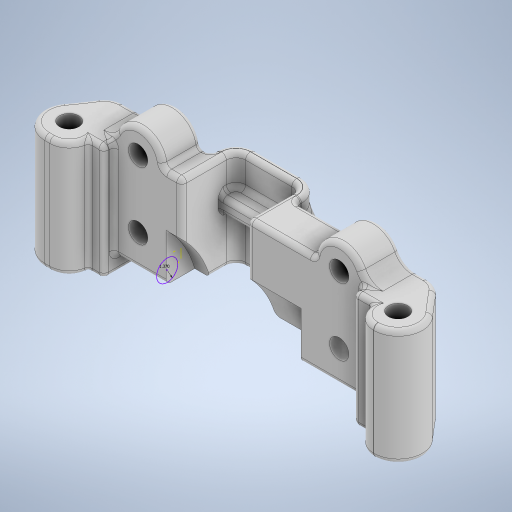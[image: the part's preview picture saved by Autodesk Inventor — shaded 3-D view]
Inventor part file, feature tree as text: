
AUTODESK INVENTOR PART (.ipt)
format: ipt  version: 2024 (Build 280153000, 153)  size: 1,158,656 bytes
history: native  units: in
note: dims shown in document units (in); Inventor stores cm internally (conversion verified against a paired STEP export)
features: fillet x17, sketch x16, extrude x13, pattern_linear x2, hole x2, projected_geometry x2, plane x1, rib x1, direct_edit x1, other x1
ambient origin geometry x8: Origin, YZ Plane, XZ Plane, XY Plane, X Axis, Y Axis, Z Axis, Center Point
bodies: Solid1 (feature_tree)
feature tree (56):
  extrude  "Extrusion1"  Depth=0.415in
  extrude  "Extrusion2"  Depth=1.62in
  fillet  "Fillet1"  Radius=0.315in
  extrude  "Extrusion3"  Depth=0.125in TaperAngle=0.0deg
  extrude  "Extrusion4"  TaperAngle=0.0deg  [1 undecoded]
  extrude  "Extrusion5"  Depth=0.25in TaperAngle=0.0deg
  fillet  "Fillet2"  Radius=0.315in
  extrude  "Extrusion6"  Depth=0.25in TaperAngle=0.0deg
  extrude  "Extrusion7"  Depth=0.55in
  pattern_linear  "Rectangular Pattern1"  Count1=2 Spacing1=0.415in
  extrude  "Extrusion8"  Depth=0.01in TaperAngle=0.0deg
  extrude  "Extrusion9"  Depth=0.3937in
  fillet  "Fillet3"  Radius=0.032in
  fillet  "Fillet4"  Radius=0.23in
  fillet  "Fillet5"  Radius=0.23in
  extrude  "Extrusion10"  Depth=0.3937in TaperAngle=0.0deg
  fillet  "Fillet6"  Radius=0.032in
  fillet  "Fillet7"  Radius=0.032in
  fillet  "Fillet8"  Radius=0.032in
  fillet  "Fillet9"  Radius=0.125in
  fillet  "Fillet10"  Radius=0.032in
  fillet  "Fillet11"  Radius=0.03in
  fillet  "Fillet12"  Radius=0.03in
  fillet  "Fillet13"  Radius=0.031in
  fillet  "Fillet14"  Radius=0.031in
  fillet  "Fillet15"  Radius=0.031in
  plane  "Work Plane1"
  rib  "Rib1"
  fillet  "Fillet16"  [1 undecoded]
  pattern_linear  "Rectangular Pattern2"  Spacing1=0.115in  [1 undecoded]
  extrude  "Extrusion11"  Depth=0.3937in
  fillet  "Fillet17"  Radius=0.031in
  hole  "Hole1"  [1 undecoded]
  hole  "Hole2"  [1 undecoded]
  extrude  "Extrusion12"  Depth=0.3937in
  extrude  "Extrusion13"  Depth=0.3937in
  direct_edit  "Direct Edit1"
  sketch  "Sketch1"  dims[d0=0.75in d1=0.415in]
  sketch  "Sketch3"  dims[d2=0.8272in d3=1.62in d4=0.315in d5=0.0in]
  sketch  "Sketch4"  dims[d6=0.315in d7=0.125in d8=0.0in]
  sketch  "Sketch5"  dims[d9=0.1575in d10=0.0in d11=0.0in]
  sketch  "Sketch6"  dims[d12=0.6375in d13=0.25in d14=0.0in d15=0.315in]
  sketch  "Sketch7"  dims[d16=0.315in d17=0.25in d18=0.0in]
  sketch  "Sketch8"  dims[d19=0.125in d20=0.55in]
  sketch  "Sketch9"  dims[d21=0.415in]
  sketch  "Sketch10"  dims[d22=0.125in]
  sketch  "Sketch11"  dims[d23=0.0625in]
  sketch  "Sketch12"  dims[d24=0.25in d25=0.0in]
  sketch  "Sketch13"  dims[d26=0.4281in]
  sketch  "Sketch14"  dims[d27=0.4281in]
  sketch  "Sketch15"  dims[d28=0.1in d29=0.0in d30=0.7874in d32=0.415in]
  sketch  "Sketch16"  dims[d34=0.0in d35=0.0in d36=0.01in d37=0.0in]
  sketch  "Sketch17"  dims[d38=0.125in d39=0.015in d40=0.032in d41=0.23in d42=0.23in d43=0.15in d44=0.0in d45=0.032in d46=0.032in d47=0.032in d48=0.125in d49=0.032in d50=0.03in d51=0.03in d52=0.031in d53=0.031in d54=0.031in d55=-0.25in d56=0.115in d57=0.1in d58=0.1in d59=0.0in d60=0.0in d61=0.1in d62=0.1in d63=0.031in d64=0.7874in d66=0.435in d67=0.0in d68=0.0in d69=0.015in d70=0.125in d71=0.75in d72=0.119in d73=0.25in d74=0.5635in d75=1.0in d76=0.8108in d77=0.125in d78=0.75in d79=0.375in d80=0.25in d81=0.5635in d82=1.0in d83=0.8108in d84=1.37in d85=0.35in d86=0.0in d87=0.1in d88=0.0in d89=3.937in d90=0.3937in d91=0.3937in d92=0.0in]
  projected_geometry  "Project Cut Edges1"
  projected_geometry  "Project Cut Edges2"
  other  "Scale1"
note: 5 required parameter values undecoded (feature->parameter linkage not recoverable at this tier; creation-order binding heuristic only, values carry confidence <= 0.55)
